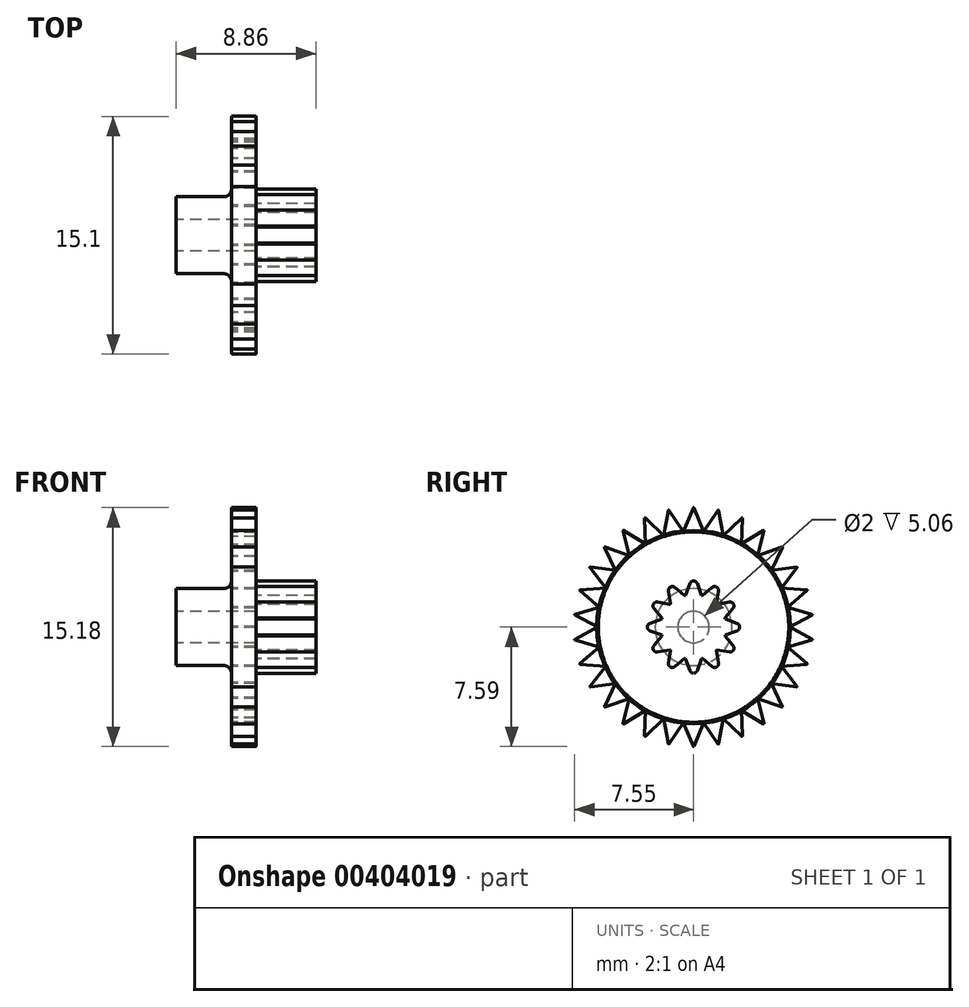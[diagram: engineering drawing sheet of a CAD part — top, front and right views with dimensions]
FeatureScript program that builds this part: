
annotation { "Feature Type Name" : "Feature", "Feature Type Description" : "" }
export const myFeature = defineFeature(function(context is Context, id is Id, definition is map)
    precondition{}
    {
        {
            var Q0;
            Q0=qCreatedBy(makeId("Front.planeOp"),FACE);
            var sketch = newSketch(context, id + "F0", { "sketchPlane" : qUnion([Q0])});
            skLineSegment(sketch, "E0.bottom", {"start": v(-0.78, 6.15) * mm, "end": v(0.78, 6.15) * mm});
            skLineSegment(sketch, "E0.left", {"start": v(-0.78, 6.15) * mm, "end": v(-0.78, 2.44) * mm});
            skLineSegment(sketch, "E0.right", {"start": v(0.78, 6.15) * mm, "end": v(0.78, 2.08) * mm});
            skLineSegment(sketch, "E1.top", {"start": v(-0.78, 2.44) * mm, "end": v(-4.28, 2.44) * mm});
            skLineSegment(sketch, "E1.right", {"start": v(-4.28, 1) * mm, "end": v(-4.28, 2.44) * mm});
            skLineSegment(sketch, "E2.top", {"start": v(0.78, 2.08) * mm, "end": v(4.58, 2.08) * mm});
            skLineSegment(sketch, "E2.right", {"start": v(4.58, 1) * mm, "end": v(4.58, 2.08) * mm});
            skLineSegment(sketch, "E3", {"start": v(-4.28, 1) * mm, "end": v(4.58, 1) * mm});
            skLineSegment(sketch, "E4", {"start": v(-13.07, 0) * mm, "end": v(15.6, 0) * mm});
            skSolve(sketch);
        }
        {
            var Q0;
            Q0=makeQuery(id+"F0.imprint","IMPRINT",FACE,{"disambiguationData":[TD([[makeQuery(id+"F0.imprint","IMPRINT",EDGE,{"derivedFrom":sQuery(id+"F0.wireOp",EDGE,"E0.bottom")}),-1.0]])]});
            var Q1;
            Q1=sQuery(id+"F0.wireOp",EDGE,"E4");
            revolve(context, id + "F1", {"entities" : qUnion([Q0]), "axis" : qUnion([Q1]), "revolveType" : RevolveType.FULL});
        }
        {
            var Q0;
            Q0=makeQuery(id+"F1.opRevolve","SWEPT_FACE",FACE,{"disambiguationData":[OSD([sQuery(id+"F0.wireOp",EDGE,"E0.right")])]});
            var sketch = newSketch(context, id + "F2", { "sketchPlane" : qUnion([Q0])});
            skArc(sketch, "E5", {"start": v(0.5, 2.02) * mm, "mid": v(0, 2.08) * mm, "end": v(-0.5, 2.02) * mm});
            skCircle(sketch, "E6", {"center": v(0, 0) * mm, "radius": 3.41 * mm});
            skLineSegment(sketch, "E7", {"start": v(0, 3.41) * mm, "end": v(-0.5, 2.02) * mm});
            skLineSegment(sketch, "E8", {"start": v(0, 3.41) * mm, "end": v(0.5, 2.02) * mm});
            skSolve(sketch);
        }
        {
            var Q0;
            {var subQ0=sQuery(id+"F2.wireOp",EDGE,"E5");var subQ1=makeQuery(id+"F2.imprint","INTERSECT",VERTEX,{"derivedFrom":[subQ0,sQuery(id+"F2.wireOp",EDGE,"E7")]});Q0=makeQuery(id+"F2.imprint","IMPRINT",FACE,{"disambiguationData":[TD([[makeQuery(id+"F2.imprint","IMPRINT",EDGE,{"disambiguationData":[TD([[subQ1,1.0]])],"derivedFrom":subQ0}),-1.0]])]});}
            var Q1;
            {var subQ0=sQuery(id+"F2.wireOp",EDGE,"E7");Q1=makeQuery(id+"F2.imprint","IMPRINT",FACE,{"disambiguationData":[TD([[makeQuery(id+"F2.imprint","IMPRINT",EDGE,{"derivedFrom":subQ0}),1.0]])]});}
            var Q2;
            Q2=makeQuery(id+"F1.opRevolve","SWEPT_FACE",FACE,{"disambiguationData":[OSD([sQuery(id+"F0.wireOp",EDGE,"E2.right")])]});
            extrude(context, id + "F3", {"entities" : qUnion([Q0, Q1]), "operationType" : NewBodyOperationType.ADD, "endBound" : BoundingType.UP_TO_SURFACE, "endBoundEntityFace" : qUnion([Q2]), "depth" : 25 * mm});
        }
        {
            var Q0;
            Q0=makeQuery(id+"F1.opRevolve","SWEPT_BODY",BODY,{"disambiguationData":[OSD([sQuery(id+"F0.wireOp",EDGE,"E0.bottom"),sQuery(id+"F0.wireOp",EDGE,"E0.left"),sQuery(id+"F0.wireOp",EDGE,"E0.right"),sQuery(id+"F0.wireOp",EDGE,"E1.top"),sQuery(id+"F0.wireOp",EDGE,"E1.right"),sQuery(id+"F0.wireOp",EDGE,"E2.top"),sQuery(id+"F0.wireOp",EDGE,"E2.right"),sQuery(id+"F0.wireOp",EDGE,"E3")])]});
            var Q1;
            Q1=makeQuery(id+"F1.opRevolve","SWEPT_FACE",FACE,{"disambiguationData":[OSD([sQuery(id+"F0.wireOp",EDGE,"E3")])]});
            circularPattern(context, id + "F4", {"operationType" : NewBodyOperationType.ADD, "entities" : qUnion([Q0]), "axis" : qUnion([Q1]), "angle" : 360 * degree, "instanceCount" : 12, "equalSpace" : true});
        }
        {
            var Q0;
            Q0=makeQuery(id+"F1.opRevolve","SWEPT_FACE",FACE,{"disambiguationData":[OSD([sQuery(id+"F0.wireOp",EDGE,"E0.left")])]});
            var sketch = newSketch(context, id + "F5", { "sketchPlane" : qUnion([Q0])});
            skCircle(sketch, "E9", {"center": v(0, 0) * mm, "radius": 7.5 * mm, "construction": true});
            skLineSegment(sketch, "E10", {"start": v(-0.67, 6.01) * mm, "end": v(-0.02, 7.58) * mm});
            skLineSegment(sketch, "E11", {"start": v(0.02, 7.58) * mm, "end": v(0.67, 6.01) * mm});
            skPoint(sketch, "E12.visualSharp", {"position": v(0, 7.62) * mm});
            skArc(sketch, "E12.filletArc", {"start": v(0.02, 7.58) * mm, "mid": v(0, 7.6) * mm, "end": v(-0.02, 7.58) * mm});
            skArc(sketch, "E13.0", {"start": v(0.67, 6.01) * mm, "mid": v(0, 6.05) * mm, "end": v(-0.67, 6.01) * mm});
            skSolve(sketch);
        }
        {
            var Q0;
            {var subQ0=sQuery(id+"F5.wireOp",EDGE,"E10");Q0=makeQuery(id+"F5.imprint","IMPRINT",FACE,{"disambiguationData":[TD([[makeQuery(id+"F5.imprint","IMPRINT",EDGE,{"derivedFrom":subQ0}),-1.0]])]});}
            var Q1;
            Q1=makeQuery(id+"F1.opRevolve","SWEPT_FACE",FACE,{"disambiguationData":[OSD([sQuery(id+"F0.wireOp",EDGE,"E0.right")])]});
            extrude(context, id + "F6", {"entities" : qUnion([Q0]), "endBound" : BoundingType.UP_TO_SURFACE, "oppositeDirection" : true, "endBoundEntityFace" : qUnion([Q1]), "depth" : 25 * mm});
        }
        {
            var Q0;
            Q0=makeQuery(id+"F3.opExtrude","SWEPT_EDGE",EDGE,{"disambiguationData":[OSD([sQuery(id+"F2.wireOp",EDGE,"E6"),sQuery(id+"F2.wireOp",EDGE,"E7"),sQuery(id+"F2.wireOp",EDGE,"E8")])]});
            var Q1;
            Q1=makeQuery(id+"F4.opPattern","COPY",EDGE,{"derivedFrom":makeQuery(id+"F3.opExtrude","SWEPT_EDGE",EDGE,{"disambiguationData":[OSD([sQuery(id+"F2.wireOp",EDGE,"E6"),sQuery(id+"F2.wireOp",EDGE,"E7"),sQuery(id+"F2.wireOp",EDGE,"E8")])]}),"instanceName":"11"});
            var Q2;
            Q2=makeQuery(id+"F4.opPattern","COPY",EDGE,{"derivedFrom":makeQuery(id+"F3.opExtrude","SWEPT_EDGE",EDGE,{"disambiguationData":[OSD([sQuery(id+"F2.wireOp",EDGE,"E6"),sQuery(id+"F2.wireOp",EDGE,"E7"),sQuery(id+"F2.wireOp",EDGE,"E8")])]}),"instanceName":"10"});
            var Q3;
            Q3=makeQuery(id+"F4.opPattern","COPY",EDGE,{"derivedFrom":makeQuery(id+"F3.opExtrude","SWEPT_EDGE",EDGE,{"disambiguationData":[OSD([sQuery(id+"F2.wireOp",EDGE,"E6"),sQuery(id+"F2.wireOp",EDGE,"E7"),sQuery(id+"F2.wireOp",EDGE,"E8")])]}),"instanceName":"9"});
            var Q4;
            Q4=makeQuery(id+"F4.opPattern","COPY",EDGE,{"derivedFrom":makeQuery(id+"F3.opExtrude","SWEPT_EDGE",EDGE,{"disambiguationData":[OSD([sQuery(id+"F2.wireOp",EDGE,"E6"),sQuery(id+"F2.wireOp",EDGE,"E7"),sQuery(id+"F2.wireOp",EDGE,"E8")])]}),"instanceName":"8"});
            var Q5;
            Q5=makeQuery(id+"F4.opPattern","COPY",EDGE,{"derivedFrom":makeQuery(id+"F3.opExtrude","SWEPT_EDGE",EDGE,{"disambiguationData":[OSD([sQuery(id+"F2.wireOp",EDGE,"E6"),sQuery(id+"F2.wireOp",EDGE,"E7"),sQuery(id+"F2.wireOp",EDGE,"E8")])]}),"instanceName":"7"});
            var Q6;
            Q6=makeQuery(id+"F4.opPattern","COPY",EDGE,{"derivedFrom":makeQuery(id+"F3.opExtrude","SWEPT_EDGE",EDGE,{"disambiguationData":[OSD([sQuery(id+"F2.wireOp",EDGE,"E6"),sQuery(id+"F2.wireOp",EDGE,"E7"),sQuery(id+"F2.wireOp",EDGE,"E8")])]}),"instanceName":"6"});
            var Q7;
            Q7=makeQuery(id+"F4.opPattern","COPY",EDGE,{"derivedFrom":makeQuery(id+"F3.opExtrude","SWEPT_EDGE",EDGE,{"disambiguationData":[OSD([sQuery(id+"F2.wireOp",EDGE,"E6"),sQuery(id+"F2.wireOp",EDGE,"E7"),sQuery(id+"F2.wireOp",EDGE,"E8")])]}),"instanceName":"5"});
            var Q8;
            Q8=makeQuery(id+"F4.opPattern","COPY",EDGE,{"derivedFrom":makeQuery(id+"F3.opExtrude","SWEPT_EDGE",EDGE,{"disambiguationData":[OSD([sQuery(id+"F2.wireOp",EDGE,"E6"),sQuery(id+"F2.wireOp",EDGE,"E7"),sQuery(id+"F2.wireOp",EDGE,"E8")])]}),"instanceName":"4"});
            var Q9;
            Q9=makeQuery(id+"F4.opPattern","COPY",EDGE,{"derivedFrom":makeQuery(id+"F3.opExtrude","SWEPT_EDGE",EDGE,{"disambiguationData":[OSD([sQuery(id+"F2.wireOp",EDGE,"E6"),sQuery(id+"F2.wireOp",EDGE,"E7"),sQuery(id+"F2.wireOp",EDGE,"E8")])]}),"instanceName":"3"});
            var Q10;
            Q10=makeQuery(id+"F4.opPattern","COPY",EDGE,{"derivedFrom":makeQuery(id+"F3.opExtrude","SWEPT_EDGE",EDGE,{"disambiguationData":[OSD([sQuery(id+"F2.wireOp",EDGE,"E6"),sQuery(id+"F2.wireOp",EDGE,"E7"),sQuery(id+"F2.wireOp",EDGE,"E8")])]}),"instanceName":"2"});
            var Q11;
            Q11=makeQuery(id+"F4.opPattern","COPY",EDGE,{"derivedFrom":makeQuery(id+"F3.opExtrude","SWEPT_EDGE",EDGE,{"disambiguationData":[OSD([sQuery(id+"F2.wireOp",EDGE,"E6"),sQuery(id+"F2.wireOp",EDGE,"E7"),sQuery(id+"F2.wireOp",EDGE,"E8")])]}),"instanceName":"1"});
            var Q12;
            {var subQ0=makeQuery(id+"F1.opRevolve","SWEPT_FACE",FACE,{"disambiguationData":[OSD([sQuery(id+"F0.wireOp",EDGE,"E2.top")])]});var subQ1=subQ0;Q12=makeQuery(id+"F4.boolean.opBoolean","INTERSECT",EDGE,{"disambiguationData":[topologyDisambiguationEdgeConnected([makeQuery(id+"F4.opPattern","COPY",FACE,{"derivedFrom":makeQuery(id+"F3.opExtrude","SWEPT_FACE",FACE,{"disambiguationData":[OSD([sQuery(id+"F2.wireOp",EDGE,"E8")])]}),"instanceName":"7"})])],"derivedFrom":[makeQuery(id+"F4.opPattern","COPY",FACE,{"derivedFrom":subQ1,"instanceName":"1"}),makeQuery(id+"F4.opPattern","COPY",FACE,{"derivedFrom":subQ1,"instanceName":"2"}),makeQuery(id+"F4.opPattern","COPY",FACE,{"derivedFrom":subQ1,"instanceName":"3"}),makeQuery(id+"F4.opPattern","COPY",FACE,{"derivedFrom":subQ1,"instanceName":"4"}),makeQuery(id+"F4.opPattern","COPY",FACE,{"derivedFrom":subQ1,"instanceName":"5"}),makeQuery(id+"F4.opPattern","COPY",FACE,{"derivedFrom":subQ1,"instanceName":"6"}),makeQuery(id+"F4.opPattern","COPY",FACE,{"derivedFrom":subQ1,"instanceName":"8"})]});}
            var Q13;
            {var subQ0=makeQuery(id+"F1.opRevolve","SWEPT_FACE",FACE,{"disambiguationData":[OSD([sQuery(id+"F0.wireOp",EDGE,"E2.top")])]});var subQ1=subQ0;Q13=makeQuery(id+"F4.boolean.opBoolean","INTERSECT",EDGE,{"disambiguationData":[topologyDisambiguationEdgeConnected([makeQuery(id+"F4.opPattern","COPY",FACE,{"derivedFrom":makeQuery(id+"F3.opExtrude","SWEPT_FACE",FACE,{"disambiguationData":[OSD([sQuery(id+"F2.wireOp",EDGE,"E7")])]}),"instanceName":"6"})])],"derivedFrom":[makeQuery(id+"F4.opPattern","COPY",FACE,{"derivedFrom":subQ1,"instanceName":"1"}),makeQuery(id+"F4.opPattern","COPY",FACE,{"derivedFrom":subQ1,"instanceName":"2"}),makeQuery(id+"F4.opPattern","COPY",FACE,{"derivedFrom":subQ1,"instanceName":"3"}),makeQuery(id+"F4.opPattern","COPY",FACE,{"derivedFrom":subQ1,"instanceName":"4"}),makeQuery(id+"F4.opPattern","COPY",FACE,{"derivedFrom":subQ1,"instanceName":"5"}),makeQuery(id+"F4.opPattern","COPY",FACE,{"derivedFrom":subQ1,"instanceName":"7"})]});}
            var Q14;
            {var subQ0=makeQuery(id+"F1.opRevolve","SWEPT_FACE",FACE,{"disambiguationData":[OSD([sQuery(id+"F0.wireOp",EDGE,"E2.top")])]});var subQ1=subQ0;Q14=makeQuery(id+"F4.boolean.opBoolean","INTERSECT",EDGE,{"disambiguationData":[topologyDisambiguationEdgeConnected([makeQuery(id+"F4.opPattern","COPY",FACE,{"derivedFrom":makeQuery(id+"F3.opExtrude","SWEPT_FACE",FACE,{"disambiguationData":[OSD([sQuery(id+"F2.wireOp",EDGE,"E8")])]}),"instanceName":"6"})])],"derivedFrom":[makeQuery(id+"F4.opPattern","COPY",FACE,{"derivedFrom":subQ1,"instanceName":"1"}),makeQuery(id+"F4.opPattern","COPY",FACE,{"derivedFrom":subQ1,"instanceName":"2"}),makeQuery(id+"F4.opPattern","COPY",FACE,{"derivedFrom":subQ1,"instanceName":"3"}),makeQuery(id+"F4.opPattern","COPY",FACE,{"derivedFrom":subQ1,"instanceName":"4"}),makeQuery(id+"F4.opPattern","COPY",FACE,{"derivedFrom":subQ1,"instanceName":"5"}),makeQuery(id+"F4.opPattern","COPY",FACE,{"derivedFrom":subQ1,"instanceName":"7"})]});}
            var Q15;
            {var subQ0=makeQuery(id+"F1.opRevolve","SWEPT_FACE",FACE,{"disambiguationData":[OSD([sQuery(id+"F0.wireOp",EDGE,"E2.top")])]});var subQ1=subQ0;Q15=makeQuery(id+"F4.boolean.opBoolean","INTERSECT",EDGE,{"disambiguationData":[topologyDisambiguationEdgeConnected([makeQuery(id+"F4.opPattern","COPY",FACE,{"derivedFrom":makeQuery(id+"F3.opExtrude","SWEPT_FACE",FACE,{"disambiguationData":[OSD([sQuery(id+"F2.wireOp",EDGE,"E7")])]}),"instanceName":"5"})])],"derivedFrom":[makeQuery(id+"F4.opPattern","COPY",FACE,{"derivedFrom":subQ1,"instanceName":"1"}),makeQuery(id+"F4.opPattern","COPY",FACE,{"derivedFrom":subQ1,"instanceName":"2"}),makeQuery(id+"F4.opPattern","COPY",FACE,{"derivedFrom":subQ1,"instanceName":"3"}),makeQuery(id+"F4.opPattern","COPY",FACE,{"derivedFrom":subQ1,"instanceName":"4"}),makeQuery(id+"F4.opPattern","COPY",FACE,{"derivedFrom":subQ1,"instanceName":"6"})]});}
            var Q16;
            {var subQ0=makeQuery(id+"F1.opRevolve","SWEPT_FACE",FACE,{"disambiguationData":[OSD([sQuery(id+"F0.wireOp",EDGE,"E2.top")])]});var subQ1=subQ0;Q16=makeQuery(id+"F4.boolean.opBoolean","INTERSECT",EDGE,{"disambiguationData":[topologyDisambiguationEdgeConnected([makeQuery(id+"F4.opPattern","COPY",FACE,{"derivedFrom":makeQuery(id+"F3.opExtrude","SWEPT_FACE",FACE,{"disambiguationData":[OSD([sQuery(id+"F2.wireOp",EDGE,"E8")])]}),"instanceName":"5"})])],"derivedFrom":[makeQuery(id+"F4.opPattern","COPY",FACE,{"derivedFrom":subQ1,"instanceName":"1"}),makeQuery(id+"F4.opPattern","COPY",FACE,{"derivedFrom":subQ1,"instanceName":"2"}),makeQuery(id+"F4.opPattern","COPY",FACE,{"derivedFrom":subQ1,"instanceName":"3"}),makeQuery(id+"F4.opPattern","COPY",FACE,{"derivedFrom":subQ1,"instanceName":"4"}),makeQuery(id+"F4.opPattern","COPY",FACE,{"derivedFrom":subQ1,"instanceName":"6"})]});}
            var Q17;
            {var subQ0=makeQuery(id+"F1.opRevolve","SWEPT_FACE",FACE,{"disambiguationData":[OSD([sQuery(id+"F0.wireOp",EDGE,"E2.top")])]});var subQ1=subQ0;Q17=makeQuery(id+"F4.boolean.opBoolean","INTERSECT",EDGE,{"disambiguationData":[topologyDisambiguationEdgeConnected([makeQuery(id+"F4.opPattern","COPY",FACE,{"derivedFrom":makeQuery(id+"F3.opExtrude","SWEPT_FACE",FACE,{"disambiguationData":[OSD([sQuery(id+"F2.wireOp",EDGE,"E7")])]}),"instanceName":"4"})])],"derivedFrom":[makeQuery(id+"F4.opPattern","COPY",FACE,{"derivedFrom":subQ1,"instanceName":"1"}),makeQuery(id+"F4.opPattern","COPY",FACE,{"derivedFrom":subQ1,"instanceName":"2"}),makeQuery(id+"F4.opPattern","COPY",FACE,{"derivedFrom":subQ1,"instanceName":"3"}),makeQuery(id+"F4.opPattern","COPY",FACE,{"derivedFrom":subQ1,"instanceName":"5"})]});}
            var Q18;
            {var subQ0=makeQuery(id+"F1.opRevolve","SWEPT_FACE",FACE,{"disambiguationData":[OSD([sQuery(id+"F0.wireOp",EDGE,"E2.top")])]});var subQ1=subQ0;Q18=makeQuery(id+"F4.boolean.opBoolean","INTERSECT",EDGE,{"disambiguationData":[topologyDisambiguationEdgeConnected([makeQuery(id+"F4.opPattern","COPY",FACE,{"derivedFrom":makeQuery(id+"F3.opExtrude","SWEPT_FACE",FACE,{"disambiguationData":[OSD([sQuery(id+"F2.wireOp",EDGE,"E8")])]}),"instanceName":"4"})])],"derivedFrom":[makeQuery(id+"F4.opPattern","COPY",FACE,{"derivedFrom":subQ1,"instanceName":"1"}),makeQuery(id+"F4.opPattern","COPY",FACE,{"derivedFrom":subQ1,"instanceName":"2"}),makeQuery(id+"F4.opPattern","COPY",FACE,{"derivedFrom":subQ1,"instanceName":"3"}),makeQuery(id+"F4.opPattern","COPY",FACE,{"derivedFrom":subQ1,"instanceName":"5"})]});}
            var Q19;
            {var subQ0=makeQuery(id+"F1.opRevolve","SWEPT_FACE",FACE,{"disambiguationData":[OSD([sQuery(id+"F0.wireOp",EDGE,"E2.top")])]});var subQ1=subQ0;Q19=makeQuery(id+"F4.boolean.opBoolean","INTERSECT",EDGE,{"disambiguationData":[topologyDisambiguationEdgeConnected([makeQuery(id+"F4.opPattern","COPY",FACE,{"derivedFrom":makeQuery(id+"F3.opExtrude","SWEPT_FACE",FACE,{"disambiguationData":[OSD([sQuery(id+"F2.wireOp",EDGE,"E7")])]}),"instanceName":"3"})])],"derivedFrom":[makeQuery(id+"F4.opPattern","COPY",FACE,{"derivedFrom":subQ1,"instanceName":"1"}),makeQuery(id+"F4.opPattern","COPY",FACE,{"derivedFrom":subQ1,"instanceName":"2"}),makeQuery(id+"F4.opPattern","COPY",FACE,{"derivedFrom":subQ1,"instanceName":"4"})]});}
            var Q20;
            {var subQ0=makeQuery(id+"F1.opRevolve","SWEPT_FACE",FACE,{"disambiguationData":[OSD([sQuery(id+"F0.wireOp",EDGE,"E2.top")])]});var subQ1=subQ0;Q20=makeQuery(id+"F4.boolean.opBoolean","INTERSECT",EDGE,{"disambiguationData":[topologyDisambiguationEdgeConnected([makeQuery(id+"F4.opPattern","COPY",FACE,{"derivedFrom":makeQuery(id+"F3.opExtrude","SWEPT_FACE",FACE,{"disambiguationData":[OSD([sQuery(id+"F2.wireOp",EDGE,"E8")])]}),"instanceName":"3"})])],"derivedFrom":[makeQuery(id+"F4.opPattern","COPY",FACE,{"derivedFrom":subQ1,"instanceName":"1"}),makeQuery(id+"F4.opPattern","COPY",FACE,{"derivedFrom":subQ1,"instanceName":"2"}),makeQuery(id+"F4.opPattern","COPY",FACE,{"derivedFrom":subQ1,"instanceName":"4"})]});}
            var Q21;
            {var subQ0=makeQuery(id+"F1.opRevolve","SWEPT_FACE",FACE,{"disambiguationData":[OSD([sQuery(id+"F0.wireOp",EDGE,"E2.top")])]});var subQ1=subQ0;Q21=makeQuery(id+"F4.boolean.opBoolean","INTERSECT",EDGE,{"disambiguationData":[topologyDisambiguationEdgeConnected([makeQuery(id+"F4.opPattern","COPY",FACE,{"derivedFrom":makeQuery(id+"F3.opExtrude","SWEPT_FACE",FACE,{"disambiguationData":[OSD([sQuery(id+"F2.wireOp",EDGE,"E7")])]}),"instanceName":"2"})])],"derivedFrom":[makeQuery(id+"F4.opPattern","COPY",FACE,{"derivedFrom":subQ1,"instanceName":"1"}),makeQuery(id+"F4.opPattern","COPY",FACE,{"derivedFrom":subQ1,"instanceName":"3"})]});}
            var Q22;
            Q22=makeQuery(id+"F4.opPattern","COPY",EDGE,{"derivedFrom":makeQuery(id+"F3.opExtrude","SWEPT_EDGE",EDGE,{"disambiguationData":[OSD([sQuery(id+"F0.wireOp",EDGE,"E0.right"),sQuery(id+"F0.wireOp",EDGE,"E2.top"),sQuery(id+"F2.wireOp",EDGE,"E7"),sQuery(id+"F2.wireOp",EDGE,"E5")])]}),"instanceName":"1"});
            var Q23;
            {var subQ0=makeQuery(id+"F1.opRevolve","SWEPT_FACE",FACE,{"disambiguationData":[OSD([sQuery(id+"F0.wireOp",EDGE,"E2.top")])]});var subQ1=subQ0;Q23=makeQuery(id+"F4.boolean.opBoolean","INTERSECT",EDGE,{"disambiguationData":[topologyDisambiguationEdgeConnected([makeQuery(id+"F4.opPattern","COPY",FACE,{"derivedFrom":makeQuery(id+"F3.opExtrude","SWEPT_FACE",FACE,{"disambiguationData":[OSD([sQuery(id+"F2.wireOp",EDGE,"E8")])]}),"instanceName":"2"})])],"derivedFrom":[makeQuery(id+"F4.opPattern","COPY",FACE,{"derivedFrom":subQ1,"instanceName":"1"}),makeQuery(id+"F4.opPattern","COPY",FACE,{"derivedFrom":subQ1,"instanceName":"3"})]});}
            var Q24;
            Q24=makeQuery(id+"F4.opPattern","COPY",EDGE,{"derivedFrom":makeQuery(id+"F3.opExtrude","SWEPT_EDGE",EDGE,{"disambiguationData":[OSD([sQuery(id+"F0.wireOp",EDGE,"E0.right"),sQuery(id+"F0.wireOp",EDGE,"E2.top"),sQuery(id+"F2.wireOp",EDGE,"E8"),sQuery(id+"F2.wireOp",EDGE,"E5")])]}),"instanceName":"1"});
            var Q25;
            Q25=makeQuery(id+"F3.opExtrude","SWEPT_EDGE",EDGE,{"disambiguationData":[OSD([sQuery(id+"F0.wireOp",EDGE,"E0.right"),sQuery(id+"F0.wireOp",EDGE,"E2.top"),sQuery(id+"F2.wireOp",EDGE,"E7"),sQuery(id+"F2.wireOp",EDGE,"E5")])]});
            var Q26;
            {var subQ0=makeQuery(id+"F1.opRevolve","SWEPT_FACE",FACE,{"disambiguationData":[OSD([sQuery(id+"F0.wireOp",EDGE,"E2.top")])]});var subQ1=subQ0;Q26=makeQuery(id+"F4.boolean.opBoolean","INTERSECT",EDGE,{"disambiguationData":[topologyDisambiguationEdgeConnected([makeQuery(id+"F4.opPattern","COPY",FACE,{"derivedFrom":makeQuery(id+"F3.opExtrude","SWEPT_FACE",FACE,{"disambiguationData":[OSD([sQuery(id+"F2.wireOp",EDGE,"E7")])]}),"instanceName":"11"})])],"derivedFrom":[makeQuery(id+"F4.opPattern","COPY",FACE,{"derivedFrom":subQ1,"instanceName":"1"}),makeQuery(id+"F4.opPattern","COPY",FACE,{"derivedFrom":subQ1,"instanceName":"2"}),makeQuery(id+"F4.opPattern","COPY",FACE,{"derivedFrom":subQ1,"instanceName":"3"}),makeQuery(id+"F4.opPattern","COPY",FACE,{"derivedFrom":subQ1,"instanceName":"4"}),makeQuery(id+"F4.opPattern","COPY",FACE,{"derivedFrom":subQ1,"instanceName":"5"}),makeQuery(id+"F4.opPattern","COPY",FACE,{"derivedFrom":subQ1,"instanceName":"6"}),makeQuery(id+"F4.opPattern","COPY",FACE,{"derivedFrom":subQ1,"instanceName":"7"}),makeQuery(id+"F4.opPattern","COPY",FACE,{"derivedFrom":subQ1,"instanceName":"8"}),makeQuery(id+"F4.opPattern","COPY",FACE,{"derivedFrom":subQ1,"instanceName":"9"}),makeQuery(id+"F4.opPattern","COPY",FACE,{"derivedFrom":subQ1,"instanceName":"10"})]});}
            var Q27;
            Q27=makeQuery(id+"F3.opExtrude","SWEPT_EDGE",EDGE,{"disambiguationData":[OSD([sQuery(id+"F0.wireOp",EDGE,"E0.right"),sQuery(id+"F0.wireOp",EDGE,"E2.top"),sQuery(id+"F2.wireOp",EDGE,"E8"),sQuery(id+"F2.wireOp",EDGE,"E5")])]});
            var Q28;
            {var subQ0=makeQuery(id+"F1.opRevolve","SWEPT_FACE",FACE,{"disambiguationData":[OSD([sQuery(id+"F0.wireOp",EDGE,"E2.top")])]});var subQ1=subQ0;Q28=makeQuery(id+"F4.boolean.opBoolean","INTERSECT",EDGE,{"disambiguationData":[topologyDisambiguationEdgeConnected([makeQuery(id+"F4.opPattern","COPY",FACE,{"derivedFrom":makeQuery(id+"F3.opExtrude","SWEPT_FACE",FACE,{"disambiguationData":[OSD([sQuery(id+"F2.wireOp",EDGE,"E7")])]}),"instanceName":"10"})])],"derivedFrom":[makeQuery(id+"F4.opPattern","COPY",FACE,{"derivedFrom":subQ1,"instanceName":"1"}),makeQuery(id+"F4.opPattern","COPY",FACE,{"derivedFrom":subQ1,"instanceName":"2"}),makeQuery(id+"F4.opPattern","COPY",FACE,{"derivedFrom":subQ1,"instanceName":"3"}),makeQuery(id+"F4.opPattern","COPY",FACE,{"derivedFrom":subQ1,"instanceName":"4"}),makeQuery(id+"F4.opPattern","COPY",FACE,{"derivedFrom":subQ1,"instanceName":"5"}),makeQuery(id+"F4.opPattern","COPY",FACE,{"derivedFrom":subQ1,"instanceName":"6"}),makeQuery(id+"F4.opPattern","COPY",FACE,{"derivedFrom":subQ1,"instanceName":"7"}),makeQuery(id+"F4.opPattern","COPY",FACE,{"derivedFrom":subQ1,"instanceName":"8"}),makeQuery(id+"F4.opPattern","COPY",FACE,{"derivedFrom":subQ1,"instanceName":"9"}),makeQuery(id+"F4.opPattern","COPY",FACE,{"derivedFrom":subQ1,"instanceName":"11"})]});}
            var Q29;
            {var subQ0=makeQuery(id+"F1.opRevolve","SWEPT_FACE",FACE,{"disambiguationData":[OSD([sQuery(id+"F0.wireOp",EDGE,"E2.top")])]});var subQ1=subQ0;Q29=makeQuery(id+"F4.boolean.opBoolean","INTERSECT",EDGE,{"disambiguationData":[topologyDisambiguationEdgeConnected([makeQuery(id+"F4.opPattern","COPY",FACE,{"derivedFrom":makeQuery(id+"F3.opExtrude","SWEPT_FACE",FACE,{"disambiguationData":[OSD([sQuery(id+"F2.wireOp",EDGE,"E8")])]}),"instanceName":"11"})])],"derivedFrom":[makeQuery(id+"F4.opPattern","COPY",FACE,{"derivedFrom":subQ1,"instanceName":"1"}),makeQuery(id+"F4.opPattern","COPY",FACE,{"derivedFrom":subQ1,"instanceName":"2"}),makeQuery(id+"F4.opPattern","COPY",FACE,{"derivedFrom":subQ1,"instanceName":"3"}),makeQuery(id+"F4.opPattern","COPY",FACE,{"derivedFrom":subQ1,"instanceName":"4"}),makeQuery(id+"F4.opPattern","COPY",FACE,{"derivedFrom":subQ1,"instanceName":"5"}),makeQuery(id+"F4.opPattern","COPY",FACE,{"derivedFrom":subQ1,"instanceName":"6"}),makeQuery(id+"F4.opPattern","COPY",FACE,{"derivedFrom":subQ1,"instanceName":"7"}),makeQuery(id+"F4.opPattern","COPY",FACE,{"derivedFrom":subQ1,"instanceName":"8"}),makeQuery(id+"F4.opPattern","COPY",FACE,{"derivedFrom":subQ1,"instanceName":"9"}),makeQuery(id+"F4.opPattern","COPY",FACE,{"derivedFrom":subQ1,"instanceName":"10"})]});}
            var Q30;
            {var subQ0=makeQuery(id+"F1.opRevolve","SWEPT_FACE",FACE,{"disambiguationData":[OSD([sQuery(id+"F0.wireOp",EDGE,"E2.top")])]});var subQ1=subQ0;Q30=makeQuery(id+"F4.boolean.opBoolean","INTERSECT",EDGE,{"disambiguationData":[topologyDisambiguationEdgeConnected([makeQuery(id+"F4.opPattern","COPY",FACE,{"derivedFrom":makeQuery(id+"F3.opExtrude","SWEPT_FACE",FACE,{"disambiguationData":[OSD([sQuery(id+"F2.wireOp",EDGE,"E7")])]}),"instanceName":"9"})])],"derivedFrom":[makeQuery(id+"F4.opPattern","COPY",FACE,{"derivedFrom":subQ1,"instanceName":"1"}),makeQuery(id+"F4.opPattern","COPY",FACE,{"derivedFrom":subQ1,"instanceName":"2"}),makeQuery(id+"F4.opPattern","COPY",FACE,{"derivedFrom":subQ1,"instanceName":"3"}),makeQuery(id+"F4.opPattern","COPY",FACE,{"derivedFrom":subQ1,"instanceName":"4"}),makeQuery(id+"F4.opPattern","COPY",FACE,{"derivedFrom":subQ1,"instanceName":"5"}),makeQuery(id+"F4.opPattern","COPY",FACE,{"derivedFrom":subQ1,"instanceName":"6"}),makeQuery(id+"F4.opPattern","COPY",FACE,{"derivedFrom":subQ1,"instanceName":"7"}),makeQuery(id+"F4.opPattern","COPY",FACE,{"derivedFrom":subQ1,"instanceName":"8"}),makeQuery(id+"F4.opPattern","COPY",FACE,{"derivedFrom":subQ1,"instanceName":"10"})]});}
            var Q31;
            {var subQ0=makeQuery(id+"F1.opRevolve","SWEPT_FACE",FACE,{"disambiguationData":[OSD([sQuery(id+"F0.wireOp",EDGE,"E2.top")])]});var subQ1=subQ0;Q31=makeQuery(id+"F4.boolean.opBoolean","INTERSECT",EDGE,{"disambiguationData":[topologyDisambiguationEdgeConnected([makeQuery(id+"F4.opPattern","COPY",FACE,{"derivedFrom":makeQuery(id+"F3.opExtrude","SWEPT_FACE",FACE,{"disambiguationData":[OSD([sQuery(id+"F2.wireOp",EDGE,"E8")])]}),"instanceName":"10"})])],"derivedFrom":[makeQuery(id+"F4.opPattern","COPY",FACE,{"derivedFrom":subQ1,"instanceName":"1"}),makeQuery(id+"F4.opPattern","COPY",FACE,{"derivedFrom":subQ1,"instanceName":"2"}),makeQuery(id+"F4.opPattern","COPY",FACE,{"derivedFrom":subQ1,"instanceName":"3"}),makeQuery(id+"F4.opPattern","COPY",FACE,{"derivedFrom":subQ1,"instanceName":"4"}),makeQuery(id+"F4.opPattern","COPY",FACE,{"derivedFrom":subQ1,"instanceName":"5"}),makeQuery(id+"F4.opPattern","COPY",FACE,{"derivedFrom":subQ1,"instanceName":"6"}),makeQuery(id+"F4.opPattern","COPY",FACE,{"derivedFrom":subQ1,"instanceName":"7"}),makeQuery(id+"F4.opPattern","COPY",FACE,{"derivedFrom":subQ1,"instanceName":"8"}),makeQuery(id+"F4.opPattern","COPY",FACE,{"derivedFrom":subQ1,"instanceName":"9"}),makeQuery(id+"F4.opPattern","COPY",FACE,{"derivedFrom":subQ1,"instanceName":"11"})]});}
            var Q32;
            {var subQ0=makeQuery(id+"F1.opRevolve","SWEPT_FACE",FACE,{"disambiguationData":[OSD([sQuery(id+"F0.wireOp",EDGE,"E2.top")])]});var subQ1=subQ0;Q32=makeQuery(id+"F4.boolean.opBoolean","INTERSECT",EDGE,{"disambiguationData":[topologyDisambiguationEdgeConnected([makeQuery(id+"F4.opPattern","COPY",FACE,{"derivedFrom":makeQuery(id+"F3.opExtrude","SWEPT_FACE",FACE,{"disambiguationData":[OSD([sQuery(id+"F2.wireOp",EDGE,"E7")])]}),"instanceName":"8"})])],"derivedFrom":[makeQuery(id+"F4.opPattern","COPY",FACE,{"derivedFrom":subQ1,"instanceName":"1"}),makeQuery(id+"F4.opPattern","COPY",FACE,{"derivedFrom":subQ1,"instanceName":"2"}),makeQuery(id+"F4.opPattern","COPY",FACE,{"derivedFrom":subQ1,"instanceName":"3"}),makeQuery(id+"F4.opPattern","COPY",FACE,{"derivedFrom":subQ1,"instanceName":"4"}),makeQuery(id+"F4.opPattern","COPY",FACE,{"derivedFrom":subQ1,"instanceName":"5"}),makeQuery(id+"F4.opPattern","COPY",FACE,{"derivedFrom":subQ1,"instanceName":"6"}),makeQuery(id+"F4.opPattern","COPY",FACE,{"derivedFrom":subQ1,"instanceName":"7"}),makeQuery(id+"F4.opPattern","COPY",FACE,{"derivedFrom":subQ1,"instanceName":"9"})]});}
            var Q33;
            {var subQ0=makeQuery(id+"F1.opRevolve","SWEPT_FACE",FACE,{"disambiguationData":[OSD([sQuery(id+"F0.wireOp",EDGE,"E2.top")])]});var subQ1=subQ0;Q33=makeQuery(id+"F4.boolean.opBoolean","INTERSECT",EDGE,{"disambiguationData":[topologyDisambiguationEdgeConnected([makeQuery(id+"F4.opPattern","COPY",FACE,{"derivedFrom":makeQuery(id+"F3.opExtrude","SWEPT_FACE",FACE,{"disambiguationData":[OSD([sQuery(id+"F2.wireOp",EDGE,"E8")])]}),"instanceName":"9"})])],"derivedFrom":[makeQuery(id+"F4.opPattern","COPY",FACE,{"derivedFrom":subQ1,"instanceName":"1"}),makeQuery(id+"F4.opPattern","COPY",FACE,{"derivedFrom":subQ1,"instanceName":"2"}),makeQuery(id+"F4.opPattern","COPY",FACE,{"derivedFrom":subQ1,"instanceName":"3"}),makeQuery(id+"F4.opPattern","COPY",FACE,{"derivedFrom":subQ1,"instanceName":"4"}),makeQuery(id+"F4.opPattern","COPY",FACE,{"derivedFrom":subQ1,"instanceName":"5"}),makeQuery(id+"F4.opPattern","COPY",FACE,{"derivedFrom":subQ1,"instanceName":"6"}),makeQuery(id+"F4.opPattern","COPY",FACE,{"derivedFrom":subQ1,"instanceName":"7"}),makeQuery(id+"F4.opPattern","COPY",FACE,{"derivedFrom":subQ1,"instanceName":"8"}),makeQuery(id+"F4.opPattern","COPY",FACE,{"derivedFrom":subQ1,"instanceName":"10"})]});}
            var Q34;
            {var subQ0=makeQuery(id+"F1.opRevolve","SWEPT_FACE",FACE,{"disambiguationData":[OSD([sQuery(id+"F0.wireOp",EDGE,"E2.top")])]});var subQ1=subQ0;Q34=makeQuery(id+"F4.boolean.opBoolean","INTERSECT",EDGE,{"disambiguationData":[topologyDisambiguationEdgeConnected([makeQuery(id+"F4.opPattern","COPY",FACE,{"derivedFrom":makeQuery(id+"F3.opExtrude","SWEPT_FACE",FACE,{"disambiguationData":[OSD([sQuery(id+"F2.wireOp",EDGE,"E7")])]}),"instanceName":"7"})])],"derivedFrom":[makeQuery(id+"F4.opPattern","COPY",FACE,{"derivedFrom":subQ1,"instanceName":"1"}),makeQuery(id+"F4.opPattern","COPY",FACE,{"derivedFrom":subQ1,"instanceName":"2"}),makeQuery(id+"F4.opPattern","COPY",FACE,{"derivedFrom":subQ1,"instanceName":"3"}),makeQuery(id+"F4.opPattern","COPY",FACE,{"derivedFrom":subQ1,"instanceName":"4"}),makeQuery(id+"F4.opPattern","COPY",FACE,{"derivedFrom":subQ1,"instanceName":"5"}),makeQuery(id+"F4.opPattern","COPY",FACE,{"derivedFrom":subQ1,"instanceName":"6"}),makeQuery(id+"F4.opPattern","COPY",FACE,{"derivedFrom":subQ1,"instanceName":"8"})]});}
            var Q35;
            {var subQ0=makeQuery(id+"F1.opRevolve","SWEPT_FACE",FACE,{"disambiguationData":[OSD([sQuery(id+"F0.wireOp",EDGE,"E2.top")])]});var subQ1=subQ0;Q35=makeQuery(id+"F4.boolean.opBoolean","INTERSECT",EDGE,{"disambiguationData":[topologyDisambiguationEdgeConnected([makeQuery(id+"F4.opPattern","COPY",FACE,{"derivedFrom":makeQuery(id+"F3.opExtrude","SWEPT_FACE",FACE,{"disambiguationData":[OSD([sQuery(id+"F2.wireOp",EDGE,"E8")])]}),"instanceName":"8"})])],"derivedFrom":[makeQuery(id+"F4.opPattern","COPY",FACE,{"derivedFrom":subQ1,"instanceName":"1"}),makeQuery(id+"F4.opPattern","COPY",FACE,{"derivedFrom":subQ1,"instanceName":"2"}),makeQuery(id+"F4.opPattern","COPY",FACE,{"derivedFrom":subQ1,"instanceName":"3"}),makeQuery(id+"F4.opPattern","COPY",FACE,{"derivedFrom":subQ1,"instanceName":"4"}),makeQuery(id+"F4.opPattern","COPY",FACE,{"derivedFrom":subQ1,"instanceName":"5"}),makeQuery(id+"F4.opPattern","COPY",FACE,{"derivedFrom":subQ1,"instanceName":"6"}),makeQuery(id+"F4.opPattern","COPY",FACE,{"derivedFrom":subQ1,"instanceName":"7"}),makeQuery(id+"F4.opPattern","COPY",FACE,{"derivedFrom":subQ1,"instanceName":"9"})]});}
            fillet(context, id + "F7", {"entities" : qUnion([Q0, Q1, Q2, Q3, Q4, Q5, Q6, Q7, Q8, Q9, Q10, Q11, Q12, Q13, Q14, Q15, Q16, Q17, Q18, Q19, Q20, Q21, Q22, Q23, Q24, Q25, Q26, Q27, Q28, Q29, Q30, Q31, Q32, Q33, Q34, Q35]), "radius" : .25 * mm, "tangentPropagation" : true, "allowEdgeOverflow" : false});
        }
        {
            var Q0;
            {var subQ0=makeQuery(id+"F1.opRevolve","SWEPT_FACE",FACE,{"disambiguationData":[OSD([sQuery(id+"F0.wireOp",EDGE,"E0.right")])]});var subQ1=subQ0;Q0=makeQuery(id+"F4.boolean.opBoolean","INTERSECT",EDGE,{"disambiguationData":[topologyDisambiguationEdgeConnected([makeQuery(id+"F4.opPattern","COPY",FACE,{"derivedFrom":makeQuery(id+"F3.opExtrude","SWEPT_FACE",FACE,{"disambiguationData":[OSD([sQuery(id+"F2.wireOp",EDGE,"E8")])]}),"instanceName":"9"})])],"derivedFrom":[makeQuery(id+"F4.opPattern","COPY",FACE,{"derivedFrom":subQ1,"instanceName":"1"}),makeQuery(id+"F4.opPattern","COPY",FACE,{"derivedFrom":subQ1,"instanceName":"2"}),makeQuery(id+"F4.opPattern","COPY",FACE,{"derivedFrom":subQ1,"instanceName":"3"}),makeQuery(id+"F4.opPattern","COPY",FACE,{"derivedFrom":subQ1,"instanceName":"4"}),makeQuery(id+"F4.opPattern","COPY",FACE,{"derivedFrom":subQ1,"instanceName":"5"}),makeQuery(id+"F4.opPattern","COPY",FACE,{"derivedFrom":subQ1,"instanceName":"6"}),makeQuery(id+"F4.opPattern","COPY",FACE,{"derivedFrom":subQ1,"instanceName":"7"}),makeQuery(id+"F4.opPattern","COPY",FACE,{"derivedFrom":subQ1,"instanceName":"8"}),makeQuery(id+"F4.opPattern","COPY",FACE,{"derivedFrom":subQ1,"instanceName":"10"})]});}
            var Q1;
            Q1=makeQuery(id+"F1.opRevolve","SWEPT_EDGE",EDGE,{"disambiguationData":[OSD([sQuery(id+"F0.wireOp",EDGE,"E0.left"),sQuery(id+"F0.wireOp",EDGE,"E1.top")])]});
            fillet(context, id + "F8", {"entities" : qUnion([Q0, Q1]), "radius" : .5 * mm, "tangentPropagation" : true, "allowEdgeOverflow" : false});
        }
        {
            var Q0;
            Q0=makeQuery(id+"F6.opExtrude","SWEPT_BODY",BODY,{"disambiguationData":[OSD([sQuery(id+"F5.wireOp",EDGE,"E10"),sQuery(id+"F5.wireOp",EDGE,"E11"),sQuery(id+"F5.wireOp",EDGE,"E12.filletArc"),sQuery(id+"F5.wireOp",EDGE,"E13.0")])]});
            var Q1;
            Q1=makeQuery(id+"F1.opRevolve","SWEPT_FACE",FACE,{"disambiguationData":[OSD([sQuery(id+"F0.wireOp",EDGE,"E0.bottom")])]});
            circularPattern(context, id + "F9", {"entities" : qUnion([Q0]), "axis" : qUnion([Q1]), "angle" : 360 * degree, "instanceCount" : 30, "equalSpace" : true});
        }
    });
